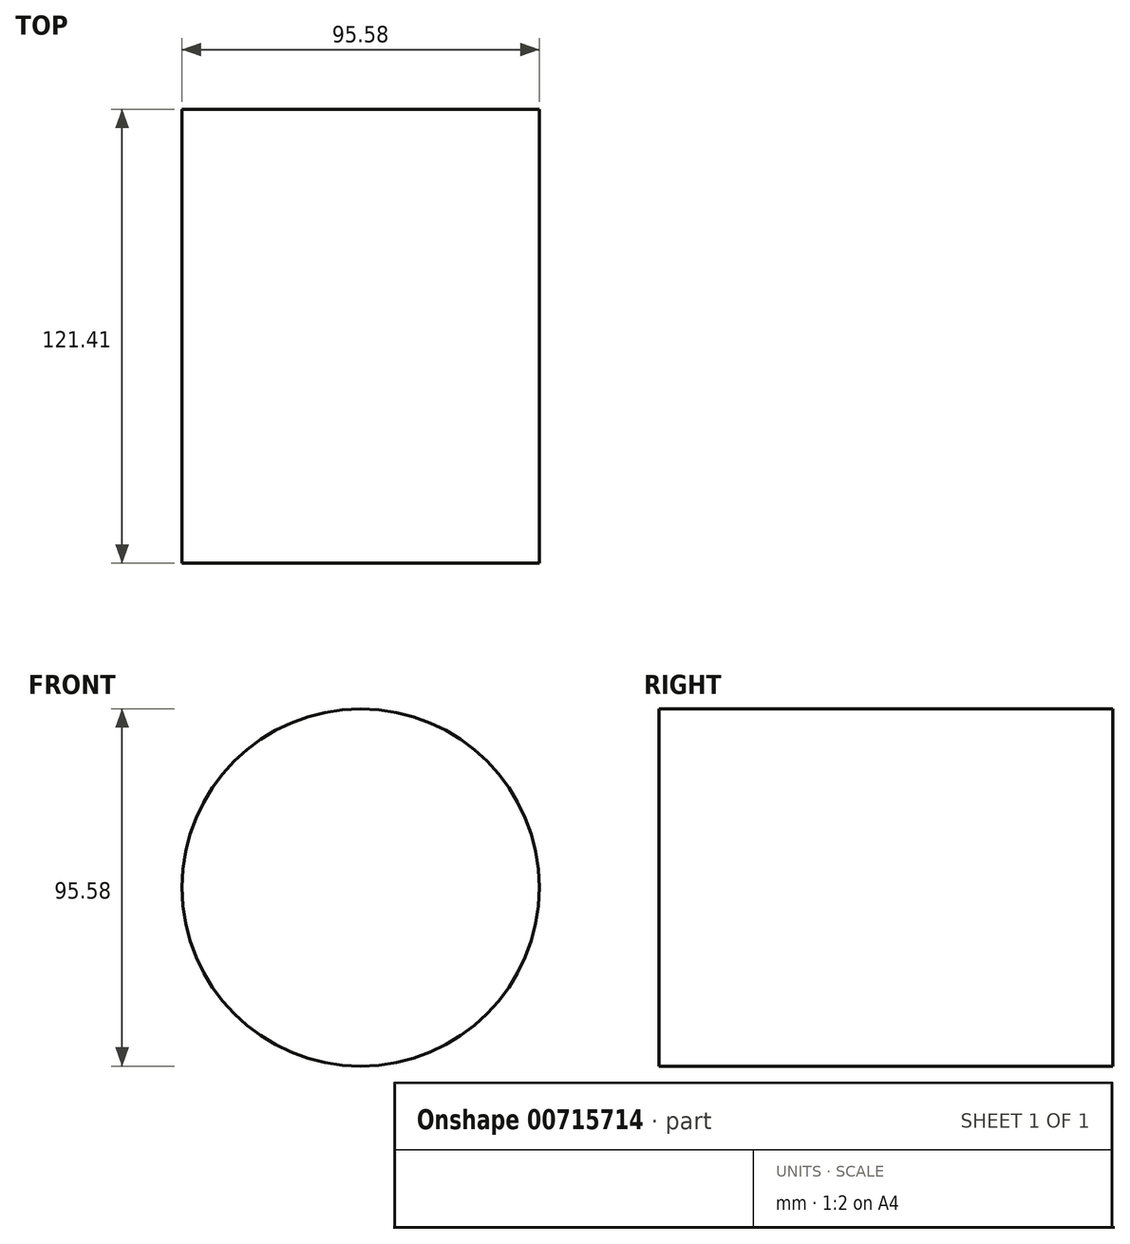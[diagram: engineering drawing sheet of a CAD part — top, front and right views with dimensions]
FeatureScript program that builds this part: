
annotation { "Feature Type Name" : "Feature", "Feature Type Description" : "" }
export const myFeature = defineFeature(function(context is Context, id is Id, definition is map)
    precondition{}
    {
        {
            var Q0;
            Q0=qCreatedBy(makeId("Front.planeOp"),FACE);
            var sketch = newSketch(context, id + "F0", { "sketchPlane" : qUnion([Q0])});
            skCircle(sketch, "E0", {"center": v(0, 0) * mm, "radius": 47.8 * mm});
            skSolve(sketch);
        }
        {
            var Q0;
            Q0 = qSketchRegion(id + "F0", true);
            extrude(context, id + "F1", {"entities" : qUnion([Q0]), "depth" : 121.4 * mm, "offsetDistance" : 25.4 * mm});
        }
    });
